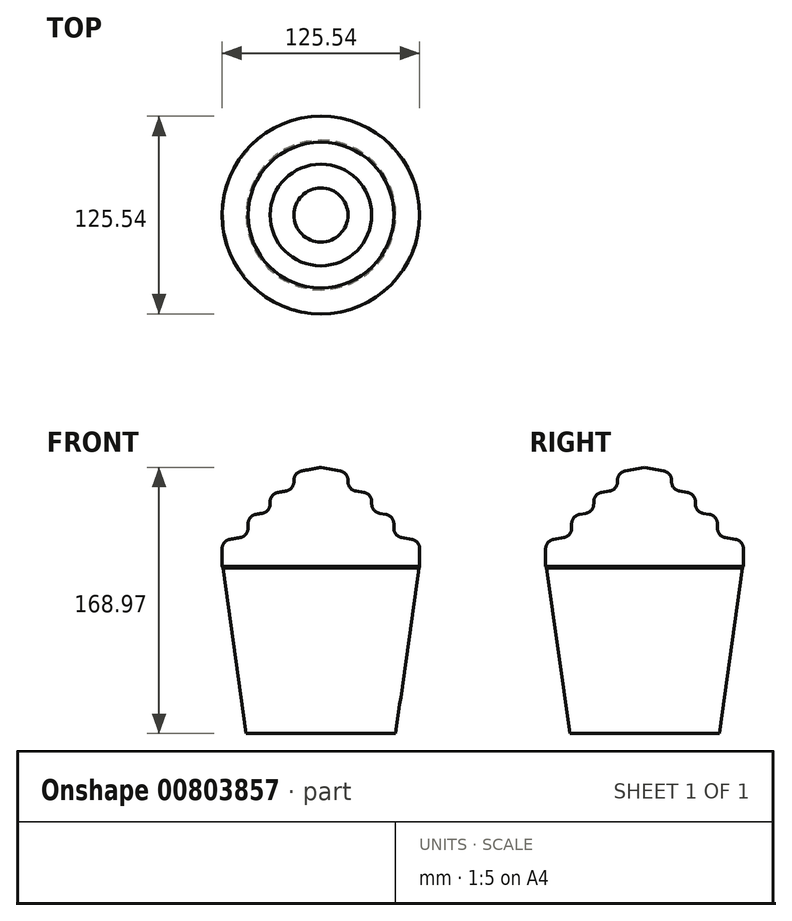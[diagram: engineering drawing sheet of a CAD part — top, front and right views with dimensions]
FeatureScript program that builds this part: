
annotation { "Feature Type Name" : "Feature", "Feature Type Description" : "" }
export const myFeature = defineFeature(function(context is Context, id is Id, definition is map)
    precondition{}
    {
        {
            var Q0;
            Q0=qCreatedBy(makeId("Top.planeOp"),FACE);
            var sketch = newSketch(context, id + "F0", { "sketchPlane" : qUnion([Q0])});
            skCircle(sketch, "E0", {"center": v(0, 0) * mm, "radius": 47.5 * mm});
            skSolve(sketch);
        }
        {
            var Q0;
            Q0 = qSketchRegion(id + "F0", true);
            extrude(context, id + "F1", {"entities" : qUnion([Q0]), "depth" : 105 * mm, "offsetDistance" : 25 * mm, "hasDraft" : true, "draftAngle" : 8 * degree});
        }
        {
            var Q0;
            Q0=qCreatedBy(makeId("Front.planeOp"),FACE);
            var sketch = newSketch(context, id + "F2", { "sketchPlane" : qUnion([Q0])});
            skLineSegment(sketch, "E1", {"start": v(0, 74.47) * mm, "end": v(0, 168.97) * mm});
            skLineSegment(sketch, "E2", {"start": v(0, 168.97) * mm, "end": v(17.17, 165.68) * mm});
            skLineSegment(sketch, "E3", {"start": v(17.17, 165.68) * mm, "end": v(17.17, 154.69) * mm});
            skLineSegment(sketch, "E4", {"start": v(17.17, 154.69) * mm, "end": v(32.28, 152.22) * mm});
            skLineSegment(sketch, "E5", {"start": v(32.28, 152.22) * mm, "end": v(32.28, 140.68) * mm});
            skLineSegment(sketch, "E6", {"start": v(32.28, 140.68) * mm, "end": v(46.29, 138.2) * mm});
            skLineSegment(sketch, "E7", {"start": v(46.29, 138.2) * mm, "end": v(46.29, 125.3) * mm});
            skLineSegment(sketch, "E8", {"start": v(46.29, 125.3) * mm, "end": v(62.77, 122.27) * mm});
            skLineSegment(sketch, "E9", {"start": v(62.77, 122.27) * mm, "end": v(62.77, 106.07) * mm});
            skLineSegment(sketch, "E10", {"start": v(62.77, 106.07) * mm, "end": v(62.22, 105.07) * mm});
            skLineSegment(sketch, "E11", {"start": v(62.22, 105.07) * mm, "end": v(0, 105.07) * mm});
            skSolve(sketch);
        }
        {
            var Q0;
            Q0 = qSketchRegion(id + "F2", true);
            var Q1;
            Q1=sQuery(id+"F2.wireOp",EDGE,"E1");
            revolve(context, id + "F3", {"surfaceOperationType" : NewSurfaceOperationType.NEW, "entities" : qUnion([Q0]), "axis" : qUnion([Q1]), "revolveType" : RevolveType.FULL});
        }
        {
            var Q0;
            Q0=makeQuery(id+"F3.opRevolve","SWEPT_EDGE",EDGE,{"disambiguationData":[OSD([sQuery(id+"F2.wireOp",EDGE,"E3"),sQuery(id+"F2.wireOp",EDGE,"E4")])]});
            var Q1;
            Q1=makeQuery(id+"F3.opRevolve","SWEPT_EDGE",EDGE,{"disambiguationData":[OSD([sQuery(id+"F2.wireOp",EDGE,"E4"),sQuery(id+"F2.wireOp",EDGE,"E5")])]});
            var Q2;
            Q2=makeQuery(id+"F3.opRevolve","SWEPT_EDGE",EDGE,{"disambiguationData":[OSD([sQuery(id+"F2.wireOp",EDGE,"E5"),sQuery(id+"F2.wireOp",EDGE,"E6")])]});
            var Q3;
            Q3=makeQuery(id+"F3.opRevolve","SWEPT_EDGE",EDGE,{"disambiguationData":[OSD([sQuery(id+"F2.wireOp",EDGE,"E6"),sQuery(id+"F2.wireOp",EDGE,"E7")])]});
            var Q4;
            Q4=makeQuery(id+"F3.opRevolve","SWEPT_EDGE",EDGE,{"disambiguationData":[OSD([sQuery(id+"F2.wireOp",EDGE,"E7"),sQuery(id+"F2.wireOp",EDGE,"E8")])]});
            var Q5;
            Q5=makeQuery(id+"F3.opRevolve","SWEPT_EDGE",EDGE,{"disambiguationData":[OSD([sQuery(id+"F2.wireOp",EDGE,"E8"),sQuery(id+"F2.wireOp",EDGE,"E9")])]});
            var Q6;
            Q6=makeQuery(id+"F3.opRevolve","SWEPT_EDGE",EDGE,{"disambiguationData":[OSD([sQuery(id+"F2.wireOp",EDGE,"E2"),sQuery(id+"F2.wireOp",EDGE,"E3")])]});
            fillet(context, id + "F4", {"entities" : qUnion([Q0, Q1, Q2, Q3, Q4, Q5, Q6]), "radius" : 6 * mm, "tangentPropagation" : true, "allowEdgeOverflow" : false});
        }
    });
